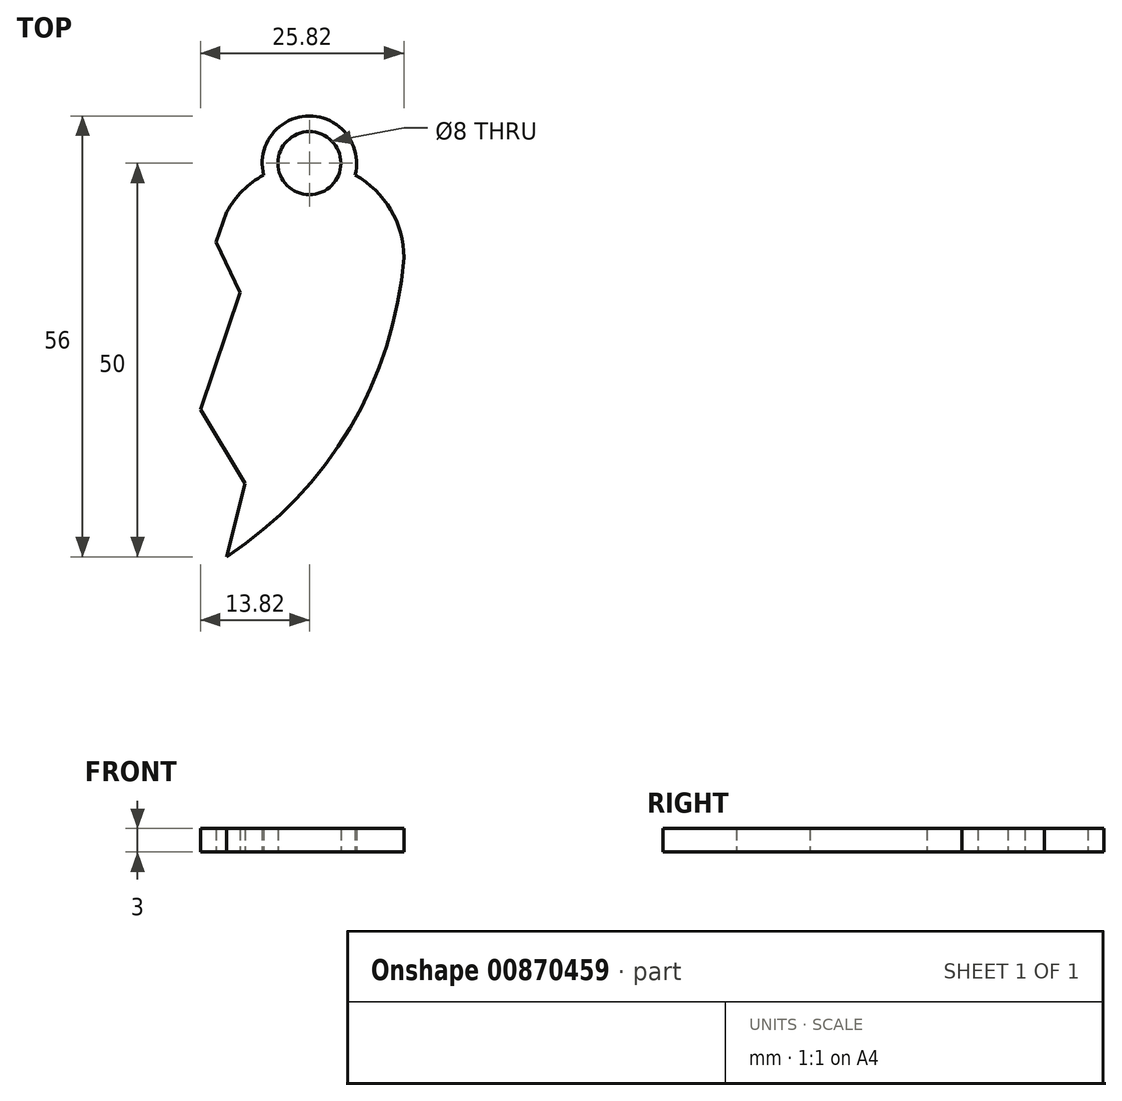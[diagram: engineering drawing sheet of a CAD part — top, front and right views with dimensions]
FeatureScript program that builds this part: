
annotation { "Feature Type Name" : "Feature", "Feature Type Description" : "" }
export const myFeature = defineFeature(function(context is Context, id is Id, definition is map)
    precondition{}
    {
        {
            var Q0;
            Q0=qCreatedBy(makeId("Top.planeOp"),FACE);
            var sketch = newSketch(context, id + "F0", { "sketchPlane" : qUnion([Q0])});
            skLineSegment(sketch, "E0", {"start": v(0, 0) * mm, "end": v(0, -20) * mm, "construction": true});
            skLineSegment(sketch, "E1", {"start": v(0, 4) * mm, "end": v(0, 0) * mm, "construction": true});
            skLineSegment(sketch, "E2", {"start": v(0, 0) * mm, "end": v(0, -10) * mm, "construction": true});
            skLineSegment(sketch, "E3", {"start": v(0, 0) * mm, "end": v(0, -2) * mm, "construction": true});
            skLineSegment(sketch, "E4", {"start": v(0, -2) * mm, "end": v(-10.5, -2) * mm, "construction": true});
            skLineSegment(sketch, "E5", {"start": v(0, -2) * mm, "end": v(10.5, -2) * mm, "construction": true});
            skPoint(sketch, "E6.centerSnap0", {"position": v(-5.25, -2) * mm});
            skLineSegment(sketch, "E7", {"start": v(0, 0) * mm, "end": v(0, -40) * mm, "construction": true});
            skCircle(sketch, "E8", {"center": v(-10.5, -2) * mm, "radius": 12 * mm});
            skCircle(sketch, "E9", {"center": v(10.5, -2) * mm, "radius": 12 * mm});
            skArc(sketch, "E10", {"start": v(-22.5, -2) * mm, "mid": v(-15.67, -23.62) * mm, "end": v(0, -40) * mm});
            skArc(sketch, "E11", {"start": v(0, -40) * mm, "mid": v(15.67, -23.62) * mm, "end": v(22.5, -2) * mm});
            skLineSegment(sketch, "E12", {"start": v(0, 3.8) * mm, "end": v(-1.33, 0) * mm});
            skLineSegment(sketch, "E13", {"start": v(-1.33, 0) * mm, "end": v(1.72, -6.43) * mm});
            skLineSegment(sketch, "E14", {"start": v(1.72, -6.43) * mm, "end": v(-3.32, -21.32) * mm});
            skLineSegment(sketch, "E15", {"start": v(-3.32, -21.32) * mm, "end": v(2.32, -30.68) * mm});
            skLineSegment(sketch, "E16", {"start": v(2.32, -30.68) * mm, "end": v(0, -40) * mm});
            skLineSegment(sketch, "E17", {"start": v(-10.5, -2) * mm, "end": v(-10.5, 10) * mm, "construction": true});
            skCircle(sketch, "E18", {"center": v(-10.5, 10) * mm, "radius": 6 * mm});
            skCircle(sketch, "E19", {"center": v(-10.5, 10) * mm, "radius": 4 * mm});
            skLineSegment(sketch, "E20", {"start": v(10.5, -2) * mm, "end": v(10.5, 10) * mm, "construction": true});
            skCircle(sketch, "E21", {"center": v(10.5, 10) * mm, "radius": 6 * mm});
            skCircle(sketch, "E22", {"center": v(10.5, 10) * mm, "radius": 4 * mm});
            skSolve(sketch);
        }
        {
            var Q0;
            {var subQ0=sQuery(id+"F0.wireOp",EDGE,"E15");Q0=makeQuery(id+"F0.imprint","IMPRINT",FACE,{"disambiguationData":[TD([[makeQuery(id+"F0.imprint","IMPRINT",EDGE,{"derivedFrom":subQ0}),1.0]])]});}
            var Q1;
            {var subQ0=sQuery(id+"F0.wireOp",EDGE,"E11");var subQ1=sQuery(id+"F0.wireOp",EDGE,"E9");var subQ5=makeQuery(id+"F0.imprint","INTERSECT",VERTEX,{"disambiguationData":[OD(0.0)],"derivedFrom":[subQ1,subQ0]});Q1=makeQuery(id+"F0.imprint","IMPRINT",FACE,{"disambiguationData":[TD([[makeQuery(id+"F0.imprint","IMPRINT",EDGE,{"disambiguationData":[TD([[subQ5,-1.0]])],"derivedFrom":subQ1}),1.0]])]});}
            var Q2;
            {var subQ0=sQuery(id+"F0.wireOp",EDGE,"E12");Q2=makeQuery(id+"F0.imprint","IMPRINT",FACE,{"disambiguationData":[TD([[makeQuery(id+"F0.imprint","IMPRINT",EDGE,{"derivedFrom":subQ0}),1.0]])]});}
            var Q3;
            {var subQ0=sQuery(id+"F0.wireOp",EDGE,"E21");var subQ1=sQuery(id+"F0.wireOp",EDGE,"E9");var subQ2=makeQuery(id+"F0.imprint","INTERSECT",VERTEX,{"disambiguationData":[OD(0.0)],"derivedFrom":[subQ1,subQ0]});Q3=makeQuery(id+"F0.imprint","IMPRINT",FACE,{"disambiguationData":[TD([[makeQuery(id+"F0.imprint","IMPRINT",EDGE,{"disambiguationData":[TD([[subQ2,-1.0]])],"derivedFrom":subQ1}),1.0]])]});}
            var Q4;
            {var subQ0=sQuery(id+"F0.wireOp",EDGE,"E21");var subQ1=sQuery(id+"F0.wireOp",EDGE,"E9");var subQ2=makeQuery(id+"F0.imprint","INTERSECT",VERTEX,{"disambiguationData":[OD(0.0)],"derivedFrom":[subQ1,subQ0]});Q4=makeQuery(id+"F0.imprint","IMPRINT",FACE,{"disambiguationData":[TD([[makeQuery(id+"F0.imprint","IMPRINT",EDGE,{"disambiguationData":[TD([[subQ2,-1.0]])],"derivedFrom":subQ1}),-1.0]])]});}
            extrude(context, id + "F1", {"entities" : qUnion([Q0, Q1, Q2, Q3, Q4]), "depth" : 3 * mm, "offsetDistance" : 25 * mm});
        }
    });
